# Revit family: P500041-141
name_source: partatom
category: Lighting Fixtures
revit_build: Autodesk Revit 2014 (Build: 20130308_1515(x64)
units: mm (PartAtom-declared; Revit-internal decimal feet)

## types (1)
- P500041-141
    Apparent Load = 100 VA
    Assembly Code = D5020200
    Color Filter = 16777215
    Connector Description = Lighting Connector
    Default Elevation = 48 "
    Description = Create a cozy home with the Briarwood Collection 1-Light Bleached Oak Farmhouse Mini-Pendant Light. A light source exudes a comforting country glow as it peeks through the X-brace design reminiscent of country barn doors and rustic farmhouse gates. A faux-wood frame coated in a rustic bleached oak finish accented by a galvanized plate on top of the structure infuses the hanging light with charming country character.
    Dimming Lamp Color Temperature Shift = <None>
    Features = Application: Ideal for any kitchen island, breakfast nook, or foyer.
Style: Perfect for coastal or farmhouse style settings.
Finish: A faux-wood frame coated in a rustic bleached oak finish accented by a galvanized plate on top of the structure infuses the hanging light with charming country character.
Materials: Constructed from steel to ensure a long product lifespan.
Glass/Shade: A light source exudes a comforting country glow as it peeks through the X-brace design reminiscent of country barn doors and rustic farmhouse gates.
Bulbs: For ideal illumination, use 1 medium base bulb that is sold separately (100w max - LED/CFL/incandescent). Compatible with dimmable bulbs.
Dimensions: Measures 10-inch width by 9-inch height by 78-inch length (installed).
Certifications: cULus dry location listed.
Pairs With: Pairs with Progress Lighting fixtures from the Durrell and Hemsworth collections.
Warranty: Our 1-Year Limited Warranty guarantees your complete satisfaction with your purchase and includes professional after-sales customer service support. Make your purchase today to breathe new life into your lighting design!
    Fixture distribution = Direct
    Glass = Paint - Hubbell - White Texture
    Gold = Hubbell - Gold
    Height = 10 "
    Housing Material = Hubbell Metal Brass
    Lamp = LED or Medium Base
    Load Classification = Lighting
    Manufacturer = Progress Lighting
    Model = P500041-141
    Photometric Web File = generic.ies
    Power Factor = 1
    Product Documentation Link = https://hubbellcdn.com
    Product Link = https://www.hubbell.com
    Square = 10 "
    Support = Paint - Hubbell - Light Silver
    Tilt Angle = -90.00°
    URL = https://www.hubbell.com
    Voltage = 120 V
    Warranty = 1 year Warranty
    Wattage Comments = 100W
    Watts = 100 W

## geometry (parser evidence)
native form markers: Sweep x3
no freeform markers — native parametric forms only
